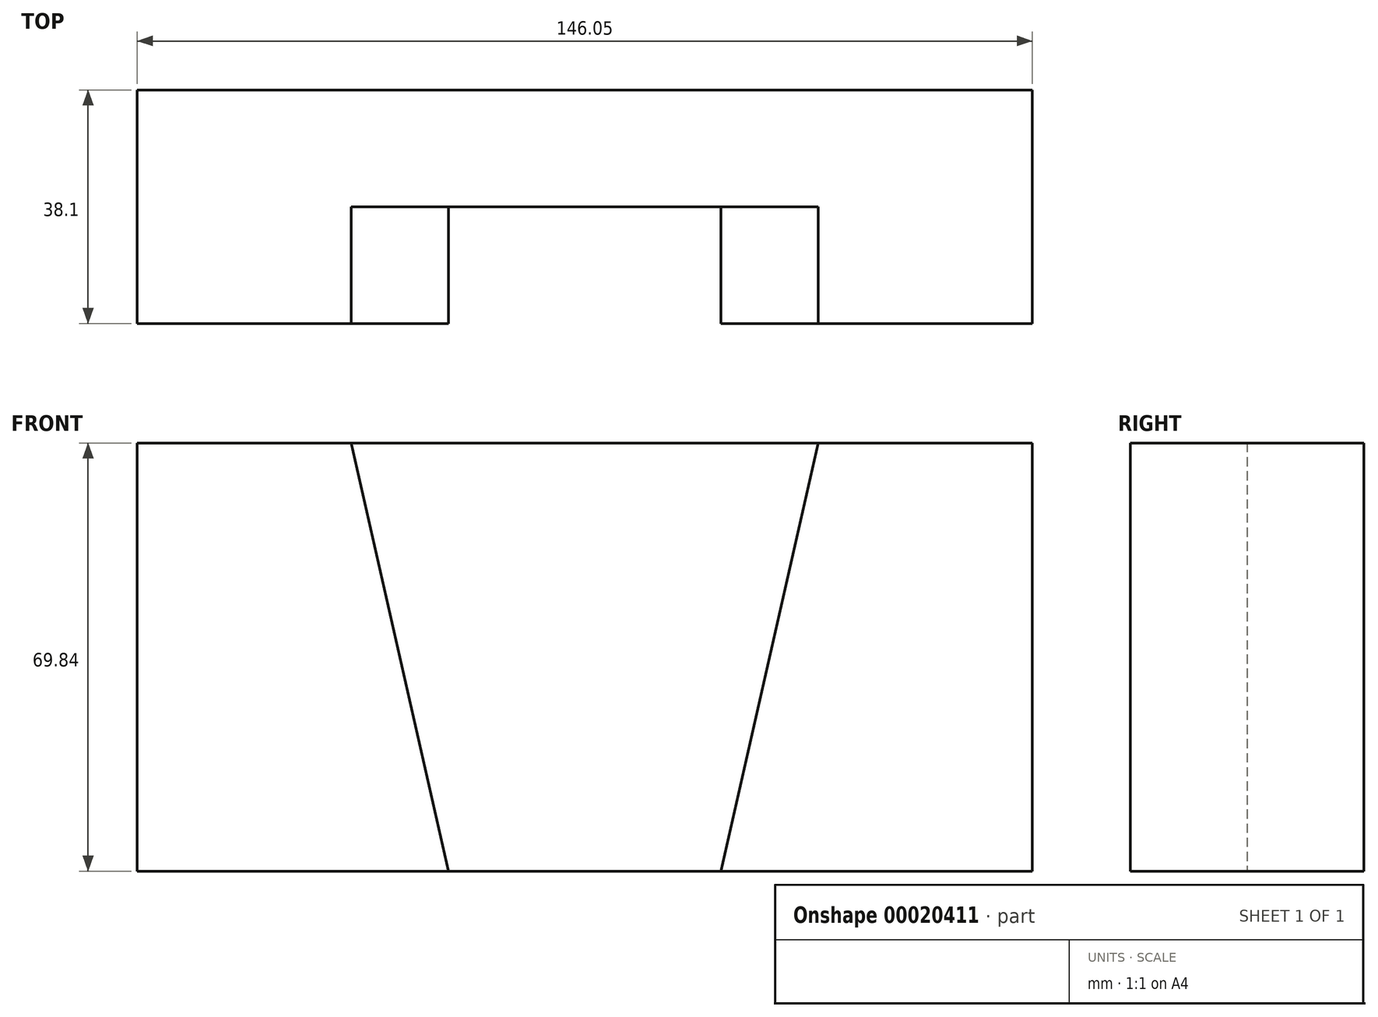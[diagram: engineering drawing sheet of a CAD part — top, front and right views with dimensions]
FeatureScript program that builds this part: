
annotation { "Feature Type Name" : "Feature", "Feature Type Description" : "" }
export const myFeature = defineFeature(function(context is Context, id is Id, definition is map)
    precondition{}
    {
        {
            var Q0;
            Q0=qCreatedBy(makeId("Front.planeOp"),FACE);
            var sketch = newSketch(context, id + "F0", { "sketchPlane" : qUnion([Q0])});
            skLineSegment(sketch, "E0.rect.bottom", {"start": v(74.27, 34.92) * mm, "end": v(-71.78, 34.93) * mm});
            skLineSegment(sketch, "E0.rect.top", {"start": v(74.27, -34.92) * mm, "end": v(-71.78, -34.92) * mm});
            skLineSegment(sketch, "E0.rect.left", {"start": v(74.27, 34.92) * mm, "end": v(74.27, -34.93) * mm});
            skLineSegment(sketch, "E0.rect.right", {"start": v(-71.78, 34.93) * mm, "end": v(-71.78, -34.92) * mm});
            skPoint(sketch, "E0.rect.middle", {"position": v(1.24, 0) * mm});
            skSolve(sketch);
        }
        {
            var Q0;
            Q0=makeQuery(id+"F0.imprint","IMPRINT",FACE,{"disambiguationData":[TD([[makeQuery(id+"F0.imprint","IMPRINT",EDGE,{"derivedFrom":sQuery(id+"F0.wireOp",EDGE,"E0.rect.bottom")}),1.0]])]});
            extrude(context, id + "F1", {"entities" : qUnion([Q0]), "depth" : 19.05 * mm});
        }
        {
            var Q0;
            Q0=makeQuery(id+"F1.opExtrude","CAP_FACE",FACE,{"disambiguationData":[OSD([sQuery(id+"F0.wireOp",EDGE,"E0.rect.bottom"),sQuery(id+"F0.wireOp",EDGE,"E0.rect.top"),sQuery(id+"F0.wireOp",EDGE,"E0.rect.left"),sQuery(id+"F0.wireOp",EDGE,"E0.rect.right")])],"isStart":false});
            var sketch = newSketch(context, id + "F2", { "sketchPlane" : qUnion([Q0])});
            skLineSegment(sketch, "E1", {"start": v(-71.78, 34.93) * mm, "end": v(-36.86, 34.93) * mm});
            skLineSegment(sketch, "E2", {"start": v(74.27, 34.92) * mm, "end": v(39.34, 34.93) * mm});
            skLineSegment(sketch, "E3", {"start": v(-71.78, 34.93) * mm, "end": v(-71.78, -34.92) * mm});
            skLineSegment(sketch, "E4", {"start": v(-71.78, -34.92) * mm, "end": v(-20.98, -34.92) * mm});
            skLineSegment(sketch, "E5", {"start": v(74.27, 34.92) * mm, "end": v(74.27, -34.93) * mm});
            skLineSegment(sketch, "E6", {"start": v(74.27, -34.93) * mm, "end": v(23.47, -34.92) * mm});
            skLineSegment(sketch, "E7", {"start": v(-36.86, 34.93) * mm, "end": v(-20.98, -34.92) * mm});
            skLineSegment(sketch, "E8", {"start": v(39.34, 34.93) * mm, "end": v(23.47, -34.92) * mm});
            skSolve(sketch);
        }
        {
            var Q0;
            Q0=makeQuery(id+"F2.imprint","IMPRINT",FACE,{"disambiguationData":[TD([[makeQuery(id+"F2.imprint","IMPRINT",EDGE,{"derivedFrom":sQuery(id+"F2.wireOp",EDGE,"E1")}),1.0]])]});
            var Q1;
            Q1=makeQuery(id+"F2.imprint","IMPRINT",FACE,{"disambiguationData":[TD([[makeQuery(id+"F2.imprint","IMPRINT",EDGE,{"derivedFrom":sQuery(id+"F2.wireOp",EDGE,"E2")}),1.0]])]});
            extrude(context, id + "F3", {"entities" : qUnion([Q0, Q1]), "operationType" : NewBodyOperationType.ADD, "depth" : 19.05 * mm});
        }
    });
